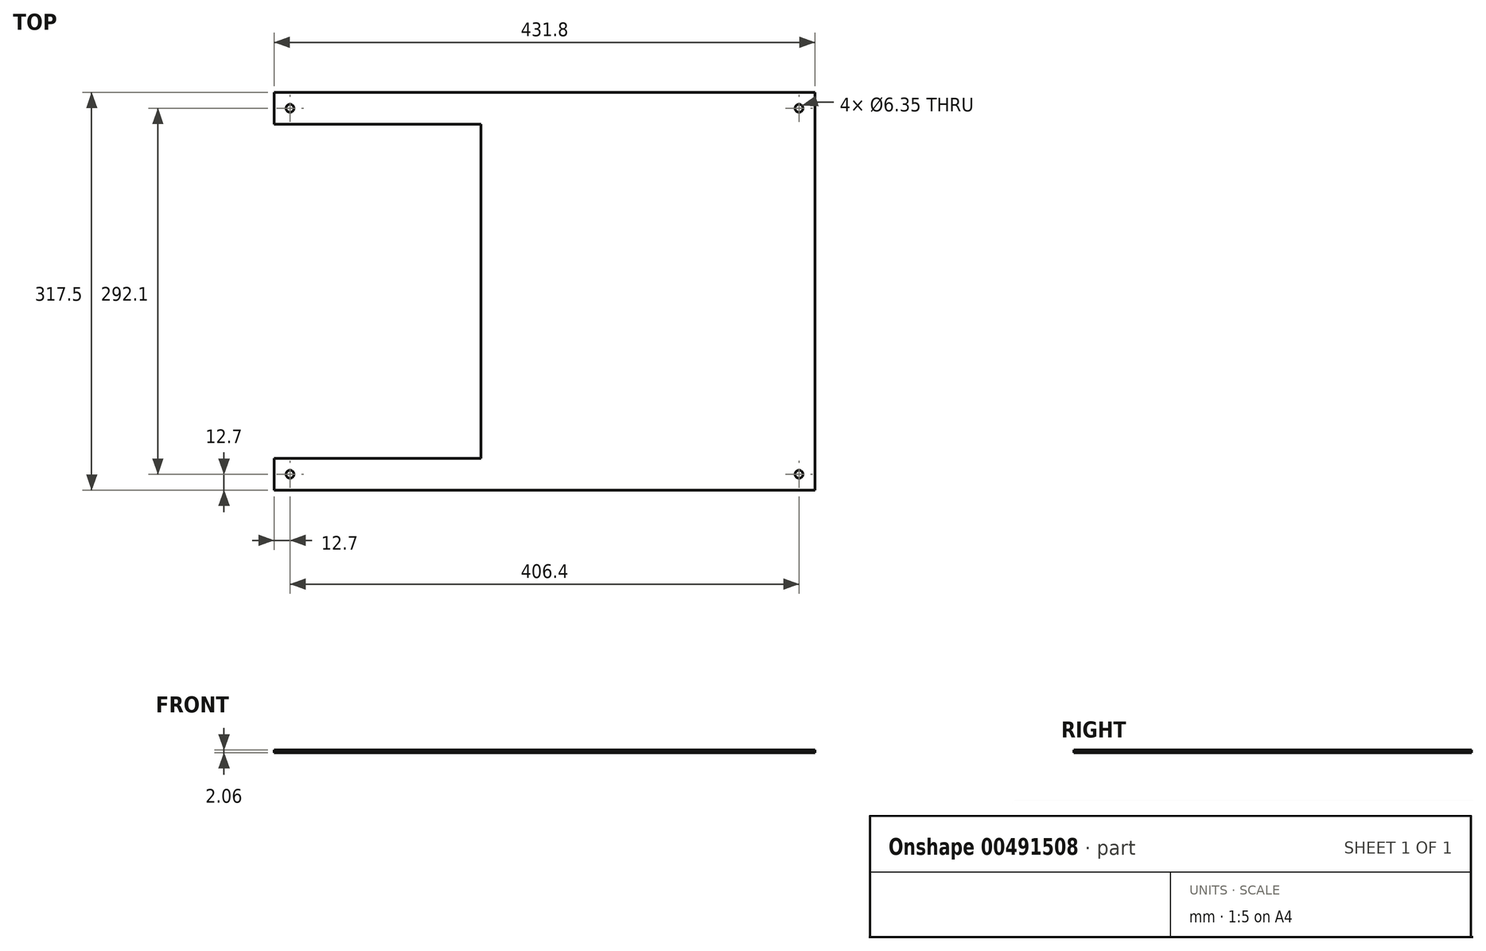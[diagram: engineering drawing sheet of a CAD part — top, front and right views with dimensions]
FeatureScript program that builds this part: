
annotation { "Feature Type Name" : "Feature", "Feature Type Description" : "" }
export const myFeature = defineFeature(function(context is Context, id is Id, definition is map)
    precondition{}
    {
        {
            var Q0;
            Q0=qCreatedBy(makeId("Top.planeOp"),FACE);
            var sketch = newSketch(context, id + "F0", { "sketchPlane" : qUnion([Q0])});
            skLineSegment(sketch, "E0.bottom", {"start": v(-215.9, 158.75) * mm, "end": v(215.9, 158.75) * mm});
            skLineSegment(sketch, "E0.top", {"start": v(-215.9, -158.75) * mm, "end": v(215.9, -158.75) * mm});
            skLineSegment(sketch, "E0.left", {"start": v(-215.9, 158.75) * mm, "end": v(-215.9, -158.75) * mm});
            skLineSegment(sketch, "E0.right", {"start": v(215.9, 158.75) * mm, "end": v(215.9, -158.75) * mm});
            skPoint(sketch, "E0.middle", {"position": v(0, 0) * mm});
            skLineSegment(sketch, "E1.bottom", {"start": v(-215.9, 133.35) * mm, "end": v(-50.8, 133.35) * mm});
            skLineSegment(sketch, "E1.top", {"start": v(-215.9, -133.35) * mm, "end": v(-50.8, -133.35) * mm});
            skLineSegment(sketch, "E1.left", {"start": v(-215.9, 133.35) * mm, "end": v(-215.9, -133.35) * mm});
            skLineSegment(sketch, "E1.right", {"start": v(-50.8, 133.35) * mm, "end": v(-50.8, -133.35) * mm});
            skCircle(sketch, "E2", {"center": v(-203.2, 146.05) * mm, "radius": 3.18 * mm});
            skCircle(sketch, "E3", {"center": v(-203.2, -146.05) * mm, "radius": 3.18 * mm});
            skCircle(sketch, "E4", {"center": v(203.2, -146.05) * mm, "radius": 3.18 * mm});
            skCircle(sketch, "E5", {"center": v(203.2, 146.05) * mm, "radius": 3.18 * mm});
            skSolve(sketch);
        }
        {
            var Q0;
            {var subQ4=sQuery(id+"F0.wireOp",EDGE,"E0.bottom");Q0=makeQuery(id+"F0.imprint","IMPRINT",FACE,{"disambiguationData":[TD([[makeQuery(id+"F0.imprint","IMPRINT",EDGE,{"derivedFrom":subQ4}),-1.0]])]});}
            extrude(context, id + "F1", {"entities" : qUnion([Q0]), "depth" : 2.06 * mm});
        }
    });
